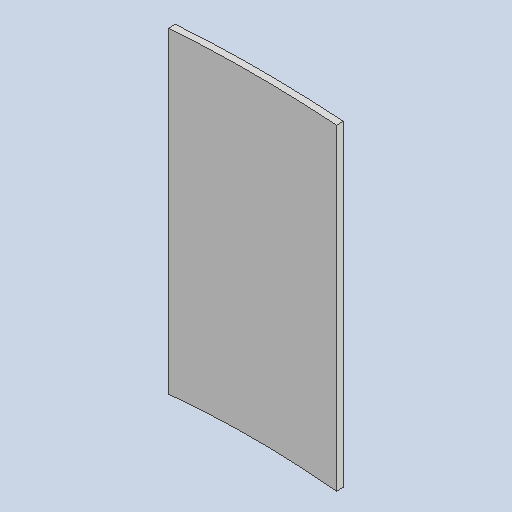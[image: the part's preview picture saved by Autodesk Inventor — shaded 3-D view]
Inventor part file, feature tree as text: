
AUTODESK INVENTOR PART (.ipt)
format: ipt  version: 2025 (Build 290162010, 162A)  size: 148,480 bytes
history: native  units: mm
features: sheet_metal_op x1, sketch x1, other x1
ambient origin geometry x8: Origin, YZ Plane, XZ Plane, XY Plane, X Axis, Y Axis, Z Axis, Center Point
bodies: Solid1 (feature_tree)
feature tree (3):
  sheet_metal_op  "Face1"
  sketch  "Sketch1"  dims[d15=2.0mm d26=512.0mm d27=50.0mm d28=700.0mm]
  other  "Plate1"
